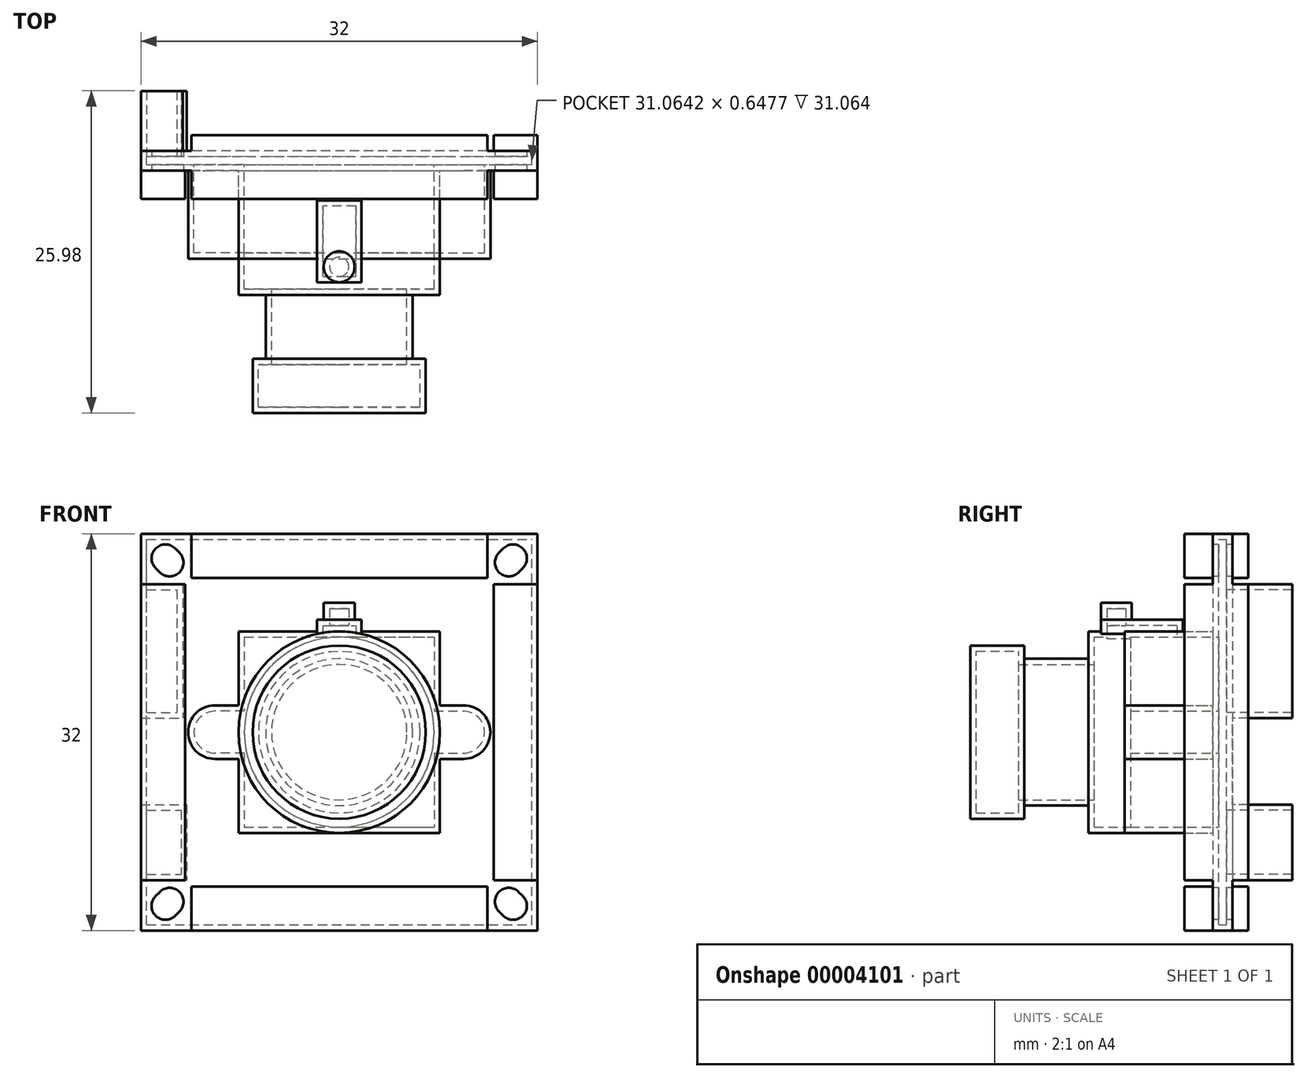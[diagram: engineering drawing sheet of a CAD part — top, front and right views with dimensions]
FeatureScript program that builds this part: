
annotation { "Feature Type Name" : "Feature", "Feature Type Description" : "" }
export const myFeature = defineFeature(function(context is Context, id is Id, definition is map)
    precondition{}
    {
        {
            var Q0;
            Q0=qCreatedBy(makeId("Front.planeOp"),FACE);
            var sketch = newSketch(context, id + "F0", { "sketchPlane" : qUnion([Q0])});
            skLineSegment(sketch, "E0.bottom", {"start": v(-16, -16) * mm, "end": v(16, -16) * mm});
            skLineSegment(sketch, "E0.top", {"start": v(-16, 16) * mm, "end": v(16, 16) * mm});
            skLineSegment(sketch, "E0.left", {"start": v(-16, -16) * mm, "end": v(-16, 16) * mm});
            skLineSegment(sketch, "E0.right", {"start": v(16, -16) * mm, "end": v(16, 16) * mm});
            skLineSegment(sketch, "E1", {"start": v(-16, -16) * mm, "end": v(16, 16) * mm});
            skSolve(sketch);
        }
        {
            var Q0;
            Q0 = qSketchRegion(id + "F0", true);
            extrude(context, id + "F1", {"entities" : qUnion([Q0]), "depth" : 1.59 * mm});
        }
        {
            var Q0;
            Q0=makeQuery(id+"F1.opExtrude","CAP_FACE",FACE,{"disambiguationData":[OSD([sQuery(id+"F0.wireOp",EDGE,"E0.bottom"),sQuery(id+"F0.wireOp",EDGE,"E0.top"),sQuery(id+"F0.wireOp",EDGE,"E0.left"),sQuery(id+"F0.wireOp",EDGE,"E0.right")])],"isStart":false});
            var sketch = newSketch(context, id + "F2", { "sketchPlane" : qUnion([Q0])});
            skLineSegment(sketch, "E2.bottom", {"start": v(-8.13, 8.13) * mm, "end": v(8.13, 8.13) * mm});
            skLineSegment(sketch, "E2.top", {"start": v(-8.13, -8.13) * mm, "end": v(8.13, -8.13) * mm});
            skLineSegment(sketch, "E2.left", {"start": v(-8.13, 8.13) * mm, "end": v(-8.13, 2.16) * mm});
            skLineSegment(sketch, "E2.right", {"start": v(8.13, 8.13) * mm, "end": v(8.13, 2.16) * mm});
            skLineSegment(sketch, "E3", {"start": v(-8.13, -8.13) * mm, "end": v(8.13, 8.13) * mm});
            skLineSegment(sketch, "E4", {"start": v(8.13, 2.16) * mm, "end": v(10.03, 2.16) * mm});
            skLineSegment(sketch, "E5", {"start": v(8.13, -2.16) * mm, "end": v(10.03, -2.16) * mm});
            skArc(sketch, "E6", {"start": v(10.03, -2.16) * mm, "mid": v(12.2, 0) * mm, "end": v(10.03, 2.16) * mm});
            skLineSegment(sketch, "E7", {"start": v(0, 0) * mm, "end": v(10.03, 0) * mm, "construction": true});
            skLineSegment(sketch, "E8.trimOffspring", {"start": v(8.13, -2.16) * mm, "end": v(8.13, -8.13) * mm});
            skLineSegment(sketch, "E9", {"start": v(0, 0) * mm, "end": v(0, 8.13) * mm});
            skLineSegment(sketch, "E10.0.MirrorCS", {"start": v(-8.13, 2.16) * mm, "end": v(-10.03, 2.16) * mm});
            skArc(sketch, "E11.0.MirrorCS", {"start": v(-10.03, -2.16) * mm, "mid": v(-12.2, 0) * mm, "end": v(-10.03, 2.16) * mm});
            skLineSegment(sketch, "E12.0.MirrorCS", {"start": v(-8.13, -2.16) * mm, "end": v(-10.03, -2.16) * mm});
            skLineSegment(sketch, "E13.trimOffspring", {"start": v(-8.13, -2.16) * mm, "end": v(-8.13, -8.13) * mm});
            skSolve(sketch);
        }
        {
            var Q0;
            Q0 = qSketchRegion(id + "F2", true);
            extrude(context, id + "F3", {"entities" : qUnion([Q0]), "operationType" : NewBodyOperationType.ADD, "depth" : 7.11 * mm});
        }
        {
            var Q0;
            Q0=makeQuery(id+"F3.opExtrude","CAP_FACE",FACE,{"disambiguationData":[OSD([sQuery(id+"F2.wireOp",EDGE,"E2.bottom"),sQuery(id+"F2.wireOp",EDGE,"E2.top"),sQuery(id+"F2.wireOp",EDGE,"E2.left"),sQuery(id+"F2.wireOp",EDGE,"E2.right"),sQuery(id+"F2.wireOp",EDGE,"E4"),sQuery(id+"F2.wireOp",EDGE,"E5"),sQuery(id+"F2.wireOp",EDGE,"E6"),sQuery(id+"F2.wireOp",EDGE,"E8.trimOffspring"),sQuery(id+"F2.wireOp",EDGE,"E10.0.MirrorCS"),sQuery(id+"F2.wireOp",EDGE,"E11.0.MirrorCS"),sQuery(id+"F2.wireOp",EDGE,"E12.0.MirrorCS"),sQuery(id+"F2.wireOp",EDGE,"E13.trimOffspring")])],"isStart":false});
            var sketch = newSketch(context, id + "F4", { "sketchPlane" : qUnion([Q0])});
            skCircle(sketch, "E14", {"center": v(0, 0) * mm, "radius": 8.13 * mm});
            skSolve(sketch);
        }
        {
            var Q0;
            Q0 = qSketchRegion(id + "F4", true);
            extrude(context, id + "F5", {"entities" : qUnion([Q0]), "operationType" : NewBodyOperationType.ADD, "depth" : 2.92 * mm});
        }
        {
            var Q0;
            Q0=makeQuery(id+"F5.opExtrude","CAP_FACE",FACE,{"disambiguationData":[OSD([sQuery(id+"F4.wireOp",EDGE,"E14")])],"isStart":false});
            var sketch = newSketch(context, id + "F6", { "sketchPlane" : qUnion([Q0])});
            skCircle(sketch, "E15", {"center": v(0, 0) * mm, "radius": 5.93 * mm});
            skSolve(sketch);
        }
        {
            var Q0;
            Q0 = qSketchRegion(id + "F6", true);
            extrude(context, id + "F7", {"entities" : qUnion([Q0]), "operationType" : NewBodyOperationType.ADD, "depth" : 5.16 * mm});
        }
        {
            var Q0;
            Q0=makeQuery(id+"F7.opExtrude","CAP_FACE",FACE,{"disambiguationData":[OSD([sQuery(id+"F6.wireOp",EDGE,"E15")])],"isStart":false});
            var sketch = newSketch(context, id + "F8", { "sketchPlane" : qUnion([Q0])});
            skCircle(sketch, "E16", {"center": v(0, 0) * mm, "radius": 6.99 * mm});
            skSolve(sketch);
        }
        {
            var Q0;
            Q0 = qSketchRegion(id + "F8", true);
            extrude(context, id + "F9", {"entities" : qUnion([Q0]), "operationType" : NewBodyOperationType.ADD, "depth" : 4.37 * mm});
        }
        {
            var Q0;
            Q0=makeQuery(id+"F3.opExtrude","SWEPT_FACE",FACE,{"disambiguationData":[OSD([sQuery(id+"F2.wireOp",EDGE,"E2.bottom")])]});
            var sketch = newSketch(context, id + "F10", { "sketchPlane" : qUnion([Q0])});
            skLineSegment(sketch, "E17.bottom", {"start": v(-1.8, -4) * mm, "end": v(1.8, -4) * mm});
            skLineSegment(sketch, "E17.top", {"start": v(-1.8, -10.6) * mm, "end": v(1.8, -10.6) * mm});
            skLineSegment(sketch, "E17.left", {"start": v(-1.8, -4) * mm, "end": v(-1.8, -10.6) * mm});
            skLineSegment(sketch, "E17.right", {"start": v(1.8, -4) * mm, "end": v(1.8, -10.6) * mm});
            skSolve(sketch);
        }
        {
            var Q0;
            Q0 = qSketchRegion(id + "F10", true);
            extrude(context, id + "F11", {"entities" : qUnion([Q0]), "operationType" : NewBodyOperationType.ADD, "depth" : 0.94 * mm, "hasSecondDirection" : true, "secondDirectionOppositeDirection" : true, "secondDirectionDepth" : 1.27 * mm});
        }
        {
            var Q0;
            Q0=makeQuery(id+"F11.opExtrude","CAP_FACE",FACE,{"disambiguationData":[OSD([sQuery(id+"F10.wireOp",EDGE,"E17.bottom"),sQuery(id+"F10.wireOp",EDGE,"E17.top"),sQuery(id+"F10.wireOp",EDGE,"E17.left"),sQuery(id+"F10.wireOp",EDGE,"E17.right")])],"isStart":false});
            var sketch = newSketch(context, id + "F12", { "sketchPlane" : qUnion([Q0])});
            skCircle(sketch, "E18", {"center": v(0, -9.36) * mm, "radius": 1.24 * mm});
            skSolve(sketch);
        }
        {
            var Q0;
            Q0 = qSketchRegion(id + "F12", true);
            extrude(context, id + "F13", {"entities" : qUnion([Q0]), "operationType" : NewBodyOperationType.ADD, "depth" : 1.37 * mm});
        }
        {
            var Q0;
            Q0=makeQuery(id+"F1.opExtrude","CAP_FACE",FACE,{"disambiguationData":[OSD([sQuery(id+"F0.wireOp",EDGE,"E0.bottom"),sQuery(id+"F0.wireOp",EDGE,"E0.top"),sQuery(id+"F0.wireOp",EDGE,"E0.left"),sQuery(id+"F0.wireOp",EDGE,"E0.right")])],"isStart":true});
            var sketch = newSketch(context, id + "F14", { "sketchPlane" : qUnion([Q0])});
            skLineSegment(sketch, "E19.bottom", {"start": v(16, 11.94) * mm, "end": v(12.62, 11.94) * mm});
            skLineSegment(sketch, "E19.top", {"start": v(16, 1.12) * mm, "end": v(12.62, 1.12) * mm});
            skLineSegment(sketch, "E19.left", {"start": v(16, 11.94) * mm, "end": v(16, 1.12) * mm});
            skLineSegment(sketch, "E19.right", {"start": v(12.62, 11.94) * mm, "end": v(12.62, 1.12) * mm});
            skLineSegment(sketch, "E20.bottom", {"start": v(16, -5.84) * mm, "end": v(12.3, -5.84) * mm});
            skLineSegment(sketch, "E20.top", {"start": v(16, -11.94) * mm, "end": v(12.3, -11.94) * mm});
            skLineSegment(sketch, "E20.left", {"start": v(16, -5.84) * mm, "end": v(16, -11.94) * mm});
            skLineSegment(sketch, "E20.right", {"start": v(12.3, -5.84) * mm, "end": v(12.3, -11.94) * mm});
            skSolve(sketch);
        }
        {
            var Q0;
            Q0 = qSketchRegion(id + "F14", true);
            extrude(context, id + "F15", {"entities" : qUnion([Q0]), "operationType" : NewBodyOperationType.ADD, "depth" : 4.83 * mm});
        }
        {
            var Q0;
            Q0=makeQuery(id+"F15.opExtrude","CAP_FACE",FACE,{"disambiguationData":[OSD([sQuery(id+"F14.wireOp",EDGE,"E19.bottom"),sQuery(id+"F14.wireOp",EDGE,"E19.top"),sQuery(id+"F14.wireOp",EDGE,"E19.left"),sQuery(id+"F14.wireOp",EDGE,"E19.right")])],"isStart":false});
            var Q1;
            Q1=makeQuery(id+"F15.opExtrude","CAP_FACE",FACE,{"disambiguationData":[OSD([sQuery(id+"F14.wireOp",EDGE,"E20.bottom"),sQuery(id+"F14.wireOp",EDGE,"E20.top"),sQuery(id+"F14.wireOp",EDGE,"E20.left"),sQuery(id+"F14.wireOp",EDGE,"E20.right")])],"isStart":false});
            shell(context, id + "F16", {"entities" : qUnion([Q0, Q1]), "thickness" : 0.47 * mm});
        }
        {
            var Q0;
            Q0=makeQuery(id+"F1.opExtrude","CAP_FACE",FACE,{"disambiguationData":[OSD([sQuery(id+"F0.wireOp",EDGE,"E0.bottom"),sQuery(id+"F0.wireOp",EDGE,"E0.top"),sQuery(id+"F0.wireOp",EDGE,"E0.left"),sQuery(id+"F0.wireOp",EDGE,"E0.right")])],"isStart":true});
            var sketch = newSketch(context, id + "F17", { "sketchPlane" : qUnion([Q0])});
            skLineSegment(sketch, "E21.bottom", {"start": v(11.94, 16) * mm, "end": v(-11.94, 16) * mm});
            skLineSegment(sketch, "E21.top", {"start": v(11.94, 12.45) * mm, "end": v(-11.94, 12.45) * mm});
            skLineSegment(sketch, "E21.left", {"start": v(11.94, 16) * mm, "end": v(11.94, 12.45) * mm});
            skLineSegment(sketch, "E21.right", {"start": v(-11.94, 16) * mm, "end": v(-11.94, 12.45) * mm});
            skLineSegment(sketch, "E22.bottom", {"start": v(-16, 11.94) * mm, "end": v(-12.45, 11.94) * mm});
            skLineSegment(sketch, "E22.top", {"start": v(-16, -11.94) * mm, "end": v(-12.45, -11.94) * mm});
            skLineSegment(sketch, "E22.left", {"start": v(-16, 11.94) * mm, "end": v(-16, -11.94) * mm});
            skLineSegment(sketch, "E22.right", {"start": v(-12.45, 11.94) * mm, "end": v(-12.45, -11.94) * mm});
            skLineSegment(sketch, "E23.bottom", {"start": v(-11.94, -16) * mm, "end": v(11.94, -16) * mm});
            skLineSegment(sketch, "E23.top", {"start": v(-11.94, -12.45) * mm, "end": v(11.94, -12.45) * mm});
            skLineSegment(sketch, "E23.left", {"start": v(-11.94, -16) * mm, "end": v(-11.94, -12.45) * mm});
            skLineSegment(sketch, "E23.right", {"start": v(11.94, -16) * mm, "end": v(11.94, -12.45) * mm});
            skSolve(sketch);
        }
        {
            var Q0;
            Q0 = qSketchRegion(id + "F17", true);
            extrude(context, id + "F18", {"entities" : qUnion([Q0]), "operationType" : NewBodyOperationType.ADD, "depth" : 1.27 * mm});
        }
        {
            var Q0;
            Q0=makeQuery(id+"F1.opExtrude","CAP_FACE",FACE,{"disambiguationData":[OSD([sQuery(id+"F0.wireOp",EDGE,"E0.bottom"),sQuery(id+"F0.wireOp",EDGE,"E0.top"),sQuery(id+"F0.wireOp",EDGE,"E0.left"),sQuery(id+"F0.wireOp",EDGE,"E0.right")])],"isStart":false});
            var sketch = newSketch(context, id + "F19", { "sketchPlane" : qUnion([Q0])});
            skLineSegment(sketch, "E24.0.0", {"start": v(11.94, 12.45) * mm, "end": v(-11.94, 12.45) * mm});
            skLineSegment(sketch, "E24.0.1", {"start": v(-11.94, 12.45) * mm, "end": v(-11.94, 16) * mm});
            skLineSegment(sketch, "E24.0.2", {"start": v(-11.94, 16) * mm, "end": v(11.94, 16) * mm});
            skLineSegment(sketch, "E24.0.3", {"start": v(11.94, 16) * mm, "end": v(11.94, 12.45) * mm});
            skLineSegment(sketch, "E25.0.0", {"start": v(12.45, 11.94) * mm, "end": v(16, 11.94) * mm});
            skLineSegment(sketch, "E25.0.1", {"start": v(16, 11.94) * mm, "end": v(16, -11.94) * mm});
            skLineSegment(sketch, "E25.0.2", {"start": v(16, -11.94) * mm, "end": v(12.45, -11.94) * mm});
            skLineSegment(sketch, "E25.0.3", {"start": v(12.45, -11.94) * mm, "end": v(12.45, 11.94) * mm});
            skLineSegment(sketch, "E26.0.0", {"start": v(-11.94, -12.45) * mm, "end": v(11.94, -12.45) * mm});
            skLineSegment(sketch, "E26.0.1", {"start": v(11.94, -12.45) * mm, "end": v(11.94, -16) * mm});
            skLineSegment(sketch, "E26.0.2", {"start": v(11.94, -16) * mm, "end": v(-11.94, -16) * mm});
            skLineSegment(sketch, "E26.0.3", {"start": v(-11.94, -16) * mm, "end": v(-11.94, -12.45) * mm});
            skLineSegment(sketch, "E27.bottom", {"start": v(-16, 11.94) * mm, "end": v(-12.45, 11.94) * mm});
            skLineSegment(sketch, "E27.top", {"start": v(-16, -11.94) * mm, "end": v(-12.45, -11.94) * mm});
            skLineSegment(sketch, "E27.left", {"start": v(-16, 11.94) * mm, "end": v(-16, -11.94) * mm});
            skLineSegment(sketch, "E27.right", {"start": v(-12.45, 11.94) * mm, "end": v(-12.45, -11.94) * mm});
            skSolve(sketch);
        }
        {
            var Q0;
            Q0 = qSketchRegion(id + "F19", true);
            extrude(context, id + "F20", {"entities" : qUnion([Q0]), "operationType" : NewBodyOperationType.ADD, "depth" : 2.3 * mm});
        }
        {
            var Q0;
            Q0=makeQuery(id+"F1.opExtrude","CAP_FACE",FACE,{"disambiguationData":[OSD([sQuery(id+"F0.wireOp",EDGE,"E0.bottom"),sQuery(id+"F0.wireOp",EDGE,"E0.top"),sQuery(id+"F0.wireOp",EDGE,"E0.left"),sQuery(id+"F0.wireOp",EDGE,"E0.right")])],"isStart":false});
            var sketch = newSketch(context, id + "F21", { "sketchPlane" : qUnion([Q0])});
            skLineSegment(sketch, "E28", {"start": v(14.47, 12.89) * mm, "end": v(14.81, 13.23) * mm});
            skLineSegment(sketch, "E29", {"start": v(12.89, 14.47) * mm, "end": v(13.23, 14.81) * mm});
            skArc(sketch, "E30", {"start": v(14.81, 13.23) * mm, "mid": v(14.81, 14.81) * mm, "end": v(13.23, 14.81) * mm});
            skArc(sketch, "E31", {"start": v(12.89, 14.47) * mm, "mid": v(12.89, 12.89) * mm, "end": v(14.47, 12.89) * mm});
            skLineSegment(sketch, "E32", {"start": v(13.68, 13.68) * mm, "end": v(16, 16) * mm, "construction": true});
            skLineSegment(sketch, "E33", {"start": v(0, 0) * mm, "end": v(0, 16) * mm, "construction": true});
            skLineSegment(sketch, "E34", {"start": v(0, 0) * mm, "end": v(10.03, 0) * mm, "construction": true});
            skArc(sketch, "E35.0.MirrorCS", {"start": v(-12.89, 14.47) * mm, "mid": v(-12.89, 12.89) * mm, "end": v(-14.47, 12.89) * mm});
            skLineSegment(sketch, "E36.0.MirrorCS", {"start": v(-12.89, 14.47) * mm, "end": v(-13.23, 14.81) * mm});
            skArc(sketch, "E37.0.MirrorCS", {"start": v(-14.81, 13.23) * mm, "mid": v(-14.81, 14.81) * mm, "end": v(-13.23, 14.81) * mm});
            skLineSegment(sketch, "E38.0.MirrorCS", {"start": v(-14.47, 12.89) * mm, "end": v(-14.81, 13.23) * mm});
            skArc(sketch, "E39.0.MirrorCS", {"start": v(-12.89, -14.47) * mm, "mid": v(-12.89, -12.89) * mm, "end": v(-14.47, -12.89) * mm});
            skLineSegment(sketch, "E40.0.MirrorCS", {"start": v(-14.47, -12.89) * mm, "end": v(-14.81, -13.23) * mm});
            skArc(sketch, "E41.0.MirrorCS", {"start": v(-14.81, -13.23) * mm, "mid": v(-14.81, -14.81) * mm, "end": v(-13.23, -14.81) * mm});
            skLineSegment(sketch, "E42.0.MirrorCS", {"start": v(-12.89, -14.47) * mm, "end": v(-13.23, -14.81) * mm});
            skArc(sketch, "E43.0.MirrorCS", {"start": v(14.81, -13.23) * mm, "mid": v(14.81, -14.81) * mm, "end": v(13.23, -14.81) * mm});
            skLineSegment(sketch, "E44.0.MirrorCS", {"start": v(14.47, -12.89) * mm, "end": v(14.81, -13.23) * mm});
            skArc(sketch, "E45.0.MirrorCS", {"start": v(12.89, -14.47) * mm, "mid": v(12.89, -12.89) * mm, "end": v(14.47, -12.89) * mm});
            skLineSegment(sketch, "E46.0.MirrorCS", {"start": v(12.89, -14.47) * mm, "end": v(13.23, -14.81) * mm});
            skSolve(sketch);
        }
        {
            var Q0;
            Q0 = qSketchRegion(id + "F21", true);
            extrude(context, id + "F22", {"entities" : qUnion([Q0]), "operationType" : NewBodyOperationType.REMOVE, "endBound" : BoundingType.THROUGH_ALL, "oppositeDirection" : true, "depth" : 25.4 * mm});
        }
    });
